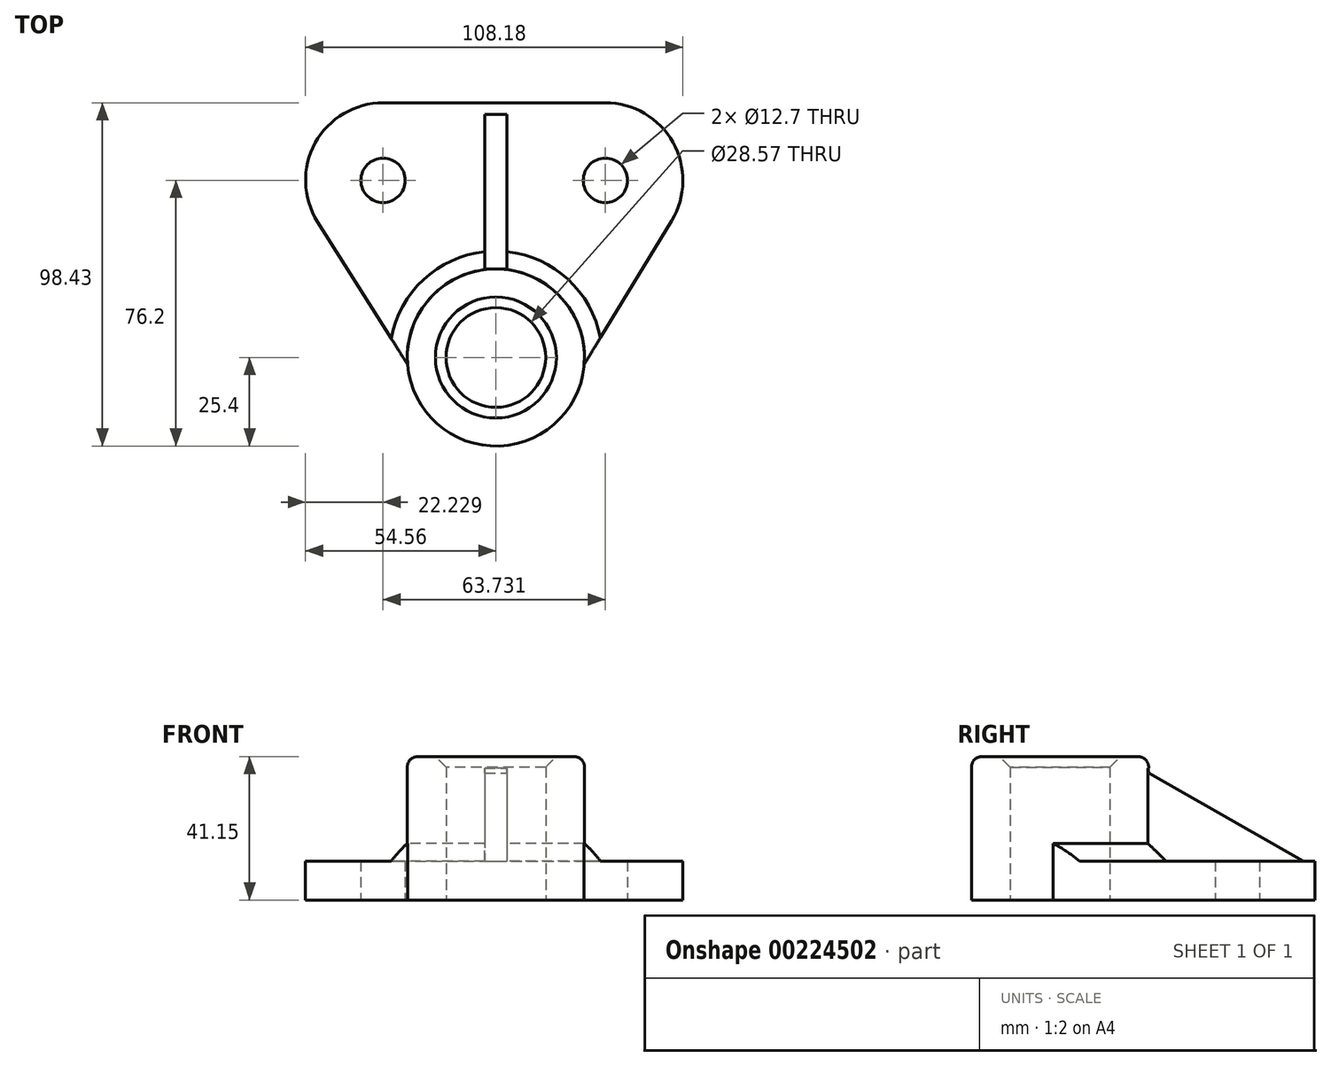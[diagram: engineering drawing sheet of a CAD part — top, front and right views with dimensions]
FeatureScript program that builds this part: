
annotation { "Feature Type Name" : "Feature", "Feature Type Description" : "" }
export const myFeature = defineFeature(function(context is Context, id is Id, definition is map)
    precondition{}
    {
        {
            var Q0;
            Q0=qCreatedBy(makeId("Top.planeOp"),FACE);
            var sketch = newSketch(context, id + "F0", { "sketchPlane" : qUnion([Q0])});
            skCircle(sketch, "E0", {"center": v(0, 0) * mm, "radius": 25.4 * mm});
            skCircle(sketch, "E1", {"center": v(-32.33, 50.8) * mm, "radius": 22.23 * mm});
            skCircle(sketch, "E2", {"center": v(31.4, 50.8) * mm, "radius": 22.23 * mm});
            skLineSegment(sketch, "E3", {"start": v(-32.33, 73.03) * mm, "end": v(31.4, 73.03) * mm});
            skCircle(sketch, "E4", {"center": v(0, 0) * mm, "radius": 14.31 * mm});
            skCircle(sketch, "E5", {"center": v(-32.33, 50.8) * mm, "radius": 6.35 * mm});
            skCircle(sketch, "E6", {"center": v(31.4, 50.8) * mm, "radius": 6.35 * mm});
            skLineSegment(sketch, "E7", {"start": v(-25.32, -2) * mm, "end": v(-51.13, 38.95) * mm});
            skLineSegment(sketch, "E8", {"start": v(25.32, -2) * mm, "end": v(50.4, 39.26) * mm});
            skSolve(sketch);
        }
        {
            var Q0;
            Q0 = qSketchRegion(id + "F0", true);
            extrude(context, id + "F1", {"entities" : qUnion([Q0]), "depth" : 11.18 * mm});
        }
        {
            var Q0;
            Q0=qCreatedBy(makeId("Top.planeOp"),FACE);
            var sketch = newSketch(context, id + "F2", { "sketchPlane" : qUnion([Q0])});
            skCircle(sketch, "E9", {"center": v(0, 0) * mm, "radius": 25.4 * mm});
            skCircle(sketch, "E10", {"center": v(0, 0) * mm, "radius": 14.29 * mm});
            skSolve(sketch);
        }
        {
            var Q0;
            Q0 = qSketchRegion(id + "F2", true);
            extrude(context, id + "F3", {"entities" : qUnion([Q0]), "operationType" : NewBodyOperationType.ADD, "depth" : 41.15 * mm});
        }
        {
            var Q0;
            Q0=makeQuery(id+"F3.opExtrude","CAP_EDGE",EDGE,{"disambiguationData":[OSD([sQuery(id+"F2.wireOp",EDGE,"E9")])],"isStart":false});
            fillet(context, id + "F4", {"entities" : qUnion([Q0]), "radius" : 3.05 * mm, "tangentPropagation" : true, "allowEdgeOverflow" : false});
        }
        {
            var Q0;
            Q0=makeQuery(id+"F1.opExtrude","CAP_FACE",FACE,{"disambiguationData":[OSD([sQuery(id+"F0.wireOp",EDGE,"E0"),sQuery(id+"F0.wireOp",EDGE,"E1"),sQuery(id+"F0.wireOp",EDGE,"E2"),sQuery(id+"F0.wireOp",EDGE,"E3"),sQuery(id+"F0.wireOp",EDGE,"E4"),sQuery(id+"F0.wireOp",EDGE,"E5"),sQuery(id+"F0.wireOp",EDGE,"E6"),sQuery(id+"F0.wireOp",EDGE,"E7"),sQuery(id+"F0.wireOp",EDGE,"E8")])],"isStart":false});
            var sketch = newSketch(context, id + "F5", { "sketchPlane" : qUnion([Q0])});
            skLineSegment(sketch, "E11", {"start": v(0, 73.03) * mm, "end": v(0, 69.72) * mm});
            skLineSegment(sketch, "E12", {"start": v(0, 69.72) * mm, "end": v(3.18, 69.72) * mm});
            skLineSegment(sketch, "E13", {"start": v(3.18, 69.72) * mm, "end": v(3.18, 25.2) * mm});
            skLineSegment(sketch, "E14", {"start": v(0, 69.72) * mm, "end": v(-3.17, 69.72) * mm});
            skLineSegment(sketch, "E15", {"start": v(-3.17, 69.72) * mm, "end": v(-3.17, 25.2) * mm});
            skSolve(sketch);
        }
        {
            var Q0;
            Q0=makeQuery(id+"F5.imprint","IMPRINT",FACE,{"disambiguationData":[TD([[makeQuery(id+"F5.imprint","IMPRINT",EDGE,{"derivedFrom":sQuery(id+"F5.wireOp",EDGE,"E12")}),-1.0]])]});
            extrude(context, id + "F6", {"entities" : qUnion([Q0]), "operationType" : NewBodyOperationType.ADD, "depth" : 26.67 * mm});
        }
        {
            var Q0;
            Q0=makeQuery(id+"F6.opExtrude","SWEPT_FACE",FACE,{"disambiguationData":[OSD([sQuery(id+"F5.wireOp",EDGE,"E13")])]});
            var sketch = newSketch(context, id + "F7", { "sketchPlane" : qUnion([Q0])});
            skLineSegment(sketch, "E16", {"start": v(25.4, 36.37) * mm, "end": v(69.72, 11.18) * mm});
            skLineSegment(sketch, "E17", {"start": v(69.72, 11.18) * mm, "end": v(69.72, 37.85) * mm});
            skLineSegment(sketch, "E18", {"start": v(25.4, 36.37) * mm, "end": v(25.2, 37.85) * mm});
            skLineSegment(sketch, "E19", {"start": v(25.2, 37.85) * mm, "end": v(69.72, 37.85) * mm});
            skSolve(sketch);
        }
        {
            var Q0;
            Q0=makeQuery(id+"F7.imprint","IMPRINT",FACE,{"disambiguationData":[TD([[makeQuery(id+"F7.imprint","IMPRINT",EDGE,{"derivedFrom":sQuery(id+"F7.wireOp",EDGE,"E16")}),1.0]])]});
            extrude(context, id + "F8", {"entities" : qUnion([Q0]), "operationType" : NewBodyOperationType.REMOVE, "oppositeDirection" : true, "depth" : 36.58 * mm});
        }
        {
            var Q0;
            Q0=makeQuery(id+"F3.opExtrude","CAP_EDGE",EDGE,{"disambiguationData":[OSD([sQuery(id+"F2.wireOp",EDGE,"E10")])],"isStart":false});
            chamfer(context, id + "F9", {"entities" : qUnion([Q0]), "width" : 3.05 * mm, "tangentPropagation" : true});
        }
        {
            var Q0;
            {var subQ0=sQuery(id+"F0.wireOp",EDGE,"E7");var subQ1=sQuery(id+"F0.wireOp",EDGE,"E0");var subQ2=makeQuery(id+"F1.opExtrude","CAP_FACE",FACE,{"disambiguationData":[OSD([subQ1,sQuery(id+"F0.wireOp",EDGE,"E1"),sQuery(id+"F0.wireOp",EDGE,"E2"),sQuery(id+"F0.wireOp",EDGE,"E3"),sQuery(id+"F0.wireOp",EDGE,"E4"),sQuery(id+"F0.wireOp",EDGE,"E5"),sQuery(id+"F0.wireOp",EDGE,"E6"),subQ0,sQuery(id+"F0.wireOp",EDGE,"E8")])],"isStart":false});var subQ3=makeQuery(id+"F3.opExtrude","SWEPT_FACE",FACE,{"disambiguationData":[OSD([sQuery(id+"F2.wireOp",EDGE,"E9")])]});Q0=makeQuery(id+"F6.boolean.opBoolean","SPLIT",EDGE,{"disambiguationData":[TD([makeQuery(id+"F1.opExtrude","SWEPT_FACE",FACE,{"disambiguationData":[OSD([subQ0])]})])],"derivedFrom":makeQuery(id+"F3.boolean.opBoolean","INTERSECT",EDGE,{"derivedFrom":[subQ2,subQ3]})});}
            var Q1;
            {var subQ0=sQuery(id+"F0.wireOp",EDGE,"E8");var subQ1=sQuery(id+"F0.wireOp",EDGE,"E0");var subQ2=makeQuery(id+"F1.opExtrude","CAP_FACE",FACE,{"disambiguationData":[OSD([subQ1,sQuery(id+"F0.wireOp",EDGE,"E1"),sQuery(id+"F0.wireOp",EDGE,"E2"),sQuery(id+"F0.wireOp",EDGE,"E3"),sQuery(id+"F0.wireOp",EDGE,"E4"),sQuery(id+"F0.wireOp",EDGE,"E5"),sQuery(id+"F0.wireOp",EDGE,"E6"),sQuery(id+"F0.wireOp",EDGE,"E7"),subQ0])],"isStart":false});var subQ3=makeQuery(id+"F3.opExtrude","SWEPT_FACE",FACE,{"disambiguationData":[OSD([sQuery(id+"F2.wireOp",EDGE,"E9")])]});Q1=makeQuery(id+"F6.boolean.opBoolean","SPLIT",EDGE,{"disambiguationData":[TD([makeQuery(id+"F1.opExtrude","SWEPT_FACE",FACE,{"disambiguationData":[OSD([subQ0])]})])],"derivedFrom":makeQuery(id+"F3.boolean.opBoolean","INTERSECT",EDGE,{"derivedFrom":[subQ2,subQ3]})});}
            chamfer(context, id + "F10", {"entities" : qUnion([Q0, Q1]), "width" : 5.08 * mm, "tangentPropagation" : true});
        }
    });
